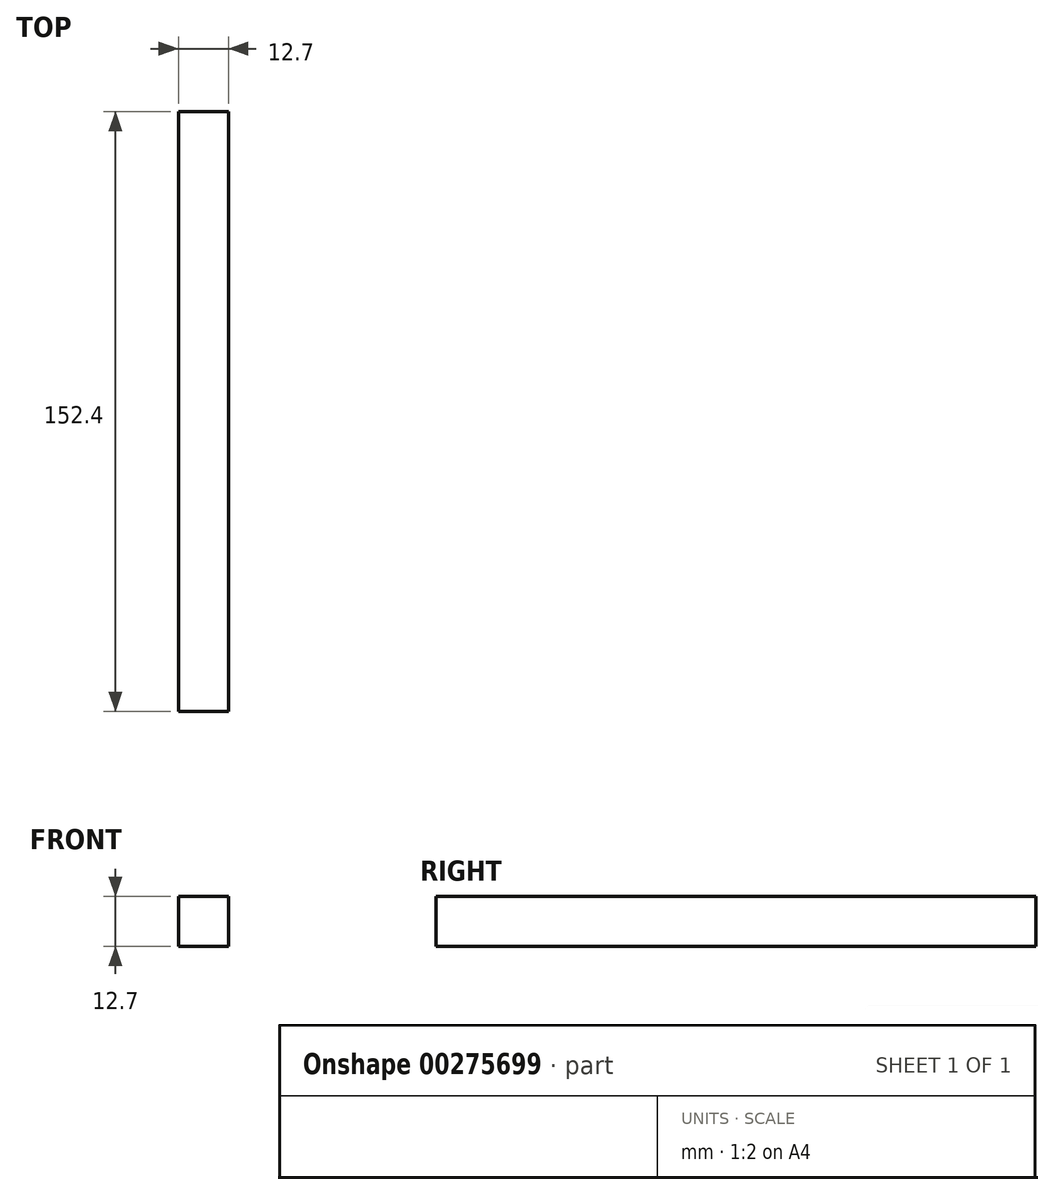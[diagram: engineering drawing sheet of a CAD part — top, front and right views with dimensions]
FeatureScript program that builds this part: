
annotation { "Feature Type Name" : "Feature", "Feature Type Description" : "" }
export const myFeature = defineFeature(function(context is Context, id is Id, definition is map)
    precondition{}
    {
        {
            var Q0;
            Q0=qCreatedBy(makeId("Front.planeOp"),FACE);
            var sketch = newSketch(context, id + "F0", { "sketchPlane" : qUnion([Q0])});
            skLineSegment(sketch, "E0.bottom", {"start": v(-110.36, 24.6) * mm, "end": v(-97.66, 24.6) * mm});
            skLineSegment(sketch, "E0.top", {"start": v(-110.36, 11.9) * mm, "end": v(-97.66, 11.9) * mm});
            skLineSegment(sketch, "E0.left", {"start": v(-110.36, 24.6) * mm, "end": v(-110.36, 11.9) * mm});
            skLineSegment(sketch, "E0.right", {"start": v(-97.66, 24.6) * mm, "end": v(-97.66, 11.9) * mm});
            skSolve(sketch);
        }
        {
            var Q0;
            Q0=makeQuery(id+"F0.imprint","IMPRINT",FACE,{"disambiguationData":[TD([[makeQuery(id+"F0.imprint","IMPRINT",EDGE,{"derivedFrom":sQuery(id+"F0.wireOp",EDGE,"E0.bottom")}),-1.0]])]});
            extrude(context, id + "F1", {"entities" : qUnion([Q0]), "depth" : 152.4 * mm});
        }
    });
